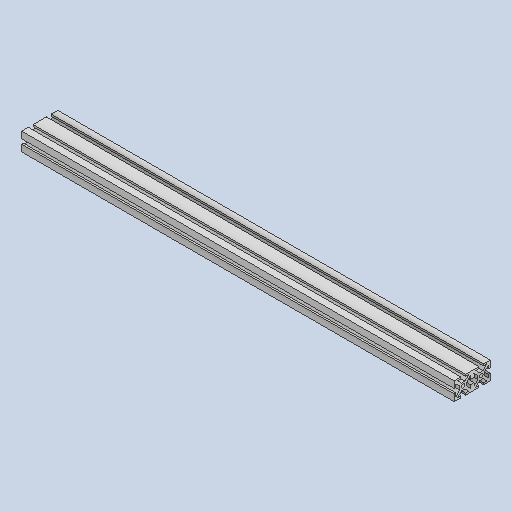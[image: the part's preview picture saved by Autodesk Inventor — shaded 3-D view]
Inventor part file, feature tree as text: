
AUTODESK INVENTOR PART (.ipt)
format: ipt  version: 2023 (Build 270158030, 158C)  size: 184,320 bytes
history: native  units: in
note: dims shown in document units (in); Inventor stores cm internally (conversion verified against a paired STEP export)
features: extrude x1, sketch x1
ambient origin geometry x8: Origin, YZ Plane, XZ Plane, XY Plane, X Axis, Y Axis, Z Axis, Center Point
bodies: Solid1 (feature_tree)
feature tree (2):
  extrude  "Extrusion1"  Depth=0.0975in
  sketch  "Sketch1"  dims[d2=0.37in d3=0.0975in d7=0.0975in d10=0.0975in d11=1.0in d13=0.0975in d16=0.0975in d17=0.37in d23=0.0975in d25=1.0in d32=0.175in d33=0.175in d35=135.0deg d36=0.175in d37=0.175in d38=0.0975in d40=0.175in d41=0.175in d42=0.175in d43=0.175in d44=0.2in d45=24.0in d46=0.0in]
